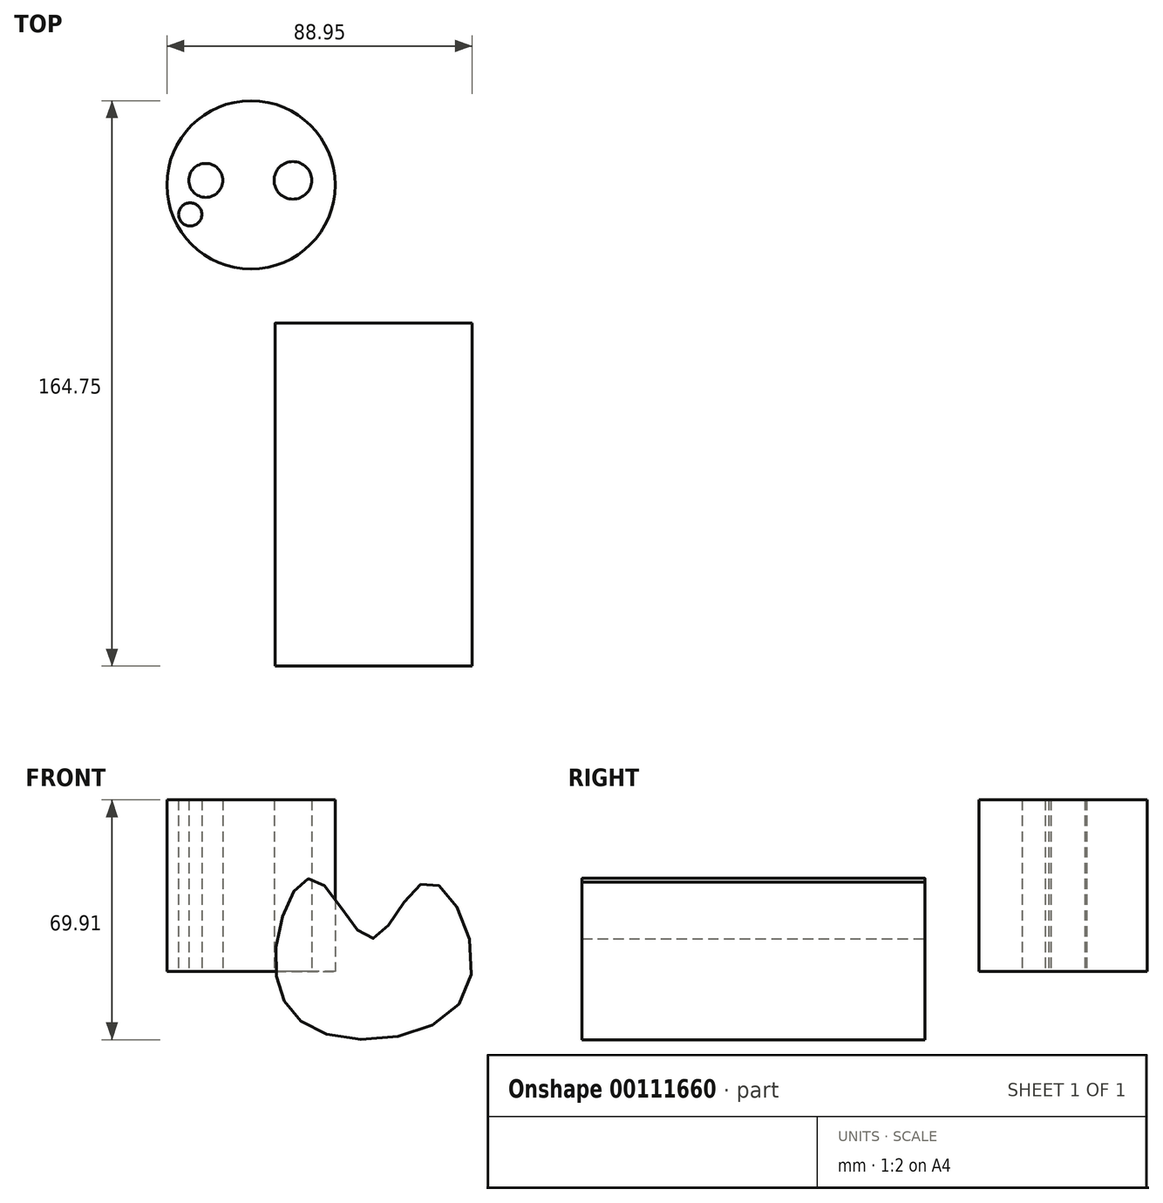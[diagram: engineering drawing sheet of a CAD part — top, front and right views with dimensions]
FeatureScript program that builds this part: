
annotation { "Feature Type Name" : "Feature", "Feature Type Description" : "" }
export const myFeature = defineFeature(function(context is Context, id is Id, definition is map)
    precondition{}
    {
        {
            var Q0;
            Q0=qCreatedBy(makeId("Top.planeOp"),FACE);
            var sketch = newSketch(context, id + "F0", { "sketchPlane" : qUnion([Q0])});
            skCircle(sketch, "E0", {"center": v(-38.95, 40.24) * mm, "radius": 24.51 * mm});
            skLineSegment(sketch, "E1", {"start": v(-55.29, 58.5) * mm, "end": v(-47.6, 52.18) * mm});
            skLineSegment(sketch, "E2", {"start": v(-47.6, 52.18) * mm, "end": v(-43.75, 56.85) * mm});
            skLineSegment(sketch, "E3", {"start": v(-43.75, 56.85) * mm, "end": v(-30.85, 48.61) * mm});
            skLineSegment(sketch, "E4", {"start": v(-30.85, 48.61) * mm, "end": v(-24.53, 52.46) * mm});
            skLineSegment(sketch, "E5", {"start": v(-24.53, 52.46) * mm, "end": v(-15.06, 45.87) * mm});
            skCircle(sketch, "E6", {"center": v(-52.14, 41.55) * mm, "radius": 4.95 * mm});
            skCircle(sketch, "E7", {"center": v(-26.74, 41.55) * mm, "radius": 5.48 * mm});
            skCircle(sketch, "E8", {"center": v(-56.67, 31.63) * mm, "radius": 3.38 * mm});
            skLineSegment(sketch, "E9", {"start": v(-56.15, 34.96) * mm, "end": v(-51.97, 32.63) * mm});
            skLineSegment(sketch, "E10", {"start": v(-57.68, 28.26) * mm, "end": v(-52.64, 26.75) * mm});
            skArc(sketch, "E11", {"start": v(-42.04, 37) * mm, "mid": v(-43.34, 32.88) * mm, "end": v(-40.02, 35.66) * mm});
            skSolve(sketch);
        }
        {
            var Q0;
            Q0=qCreatedBy(makeId("Front.planeOp"),FACE);
            var sketch = newSketch(context, id + "F1", { "sketchPlane" : qUnion([Q0])});
            skFitSpline(sketch, "E12", {"points": [v(-31.63, 7.12) * mm, v(-20.35, 26.92) * mm, v(-3.7, 9.53) * mm, v(12.2, 26) * mm, v(24.23, -5.09) * mm, v(-18.87, -17.67) * mm, v(-31.63, 7.12) * mm]});
            skSolve(sketch);
        }
        {
            var Q0;
            Q0 = qSketchRegion(id + "F1", true);
            extrude(context, id + "F2", {"entities" : qUnion([Q0]), "depth" : 100 * mm});
        }
        {
            var Q0;
            Q0=makeQuery(id+"F0.imprint","IMPRINT",FACE,{"disambiguationData":[TD([[makeQuery(id+"F0.imprint","IMPRINT",EDGE,{"derivedFrom":sQuery(id+"F0.wireOp",EDGE,"E0")}),1.0]])]});
            extrude(context, id + "F3", {"entities" : qUnion([Q0]), "depth" : 50 * mm});
        }
    });
